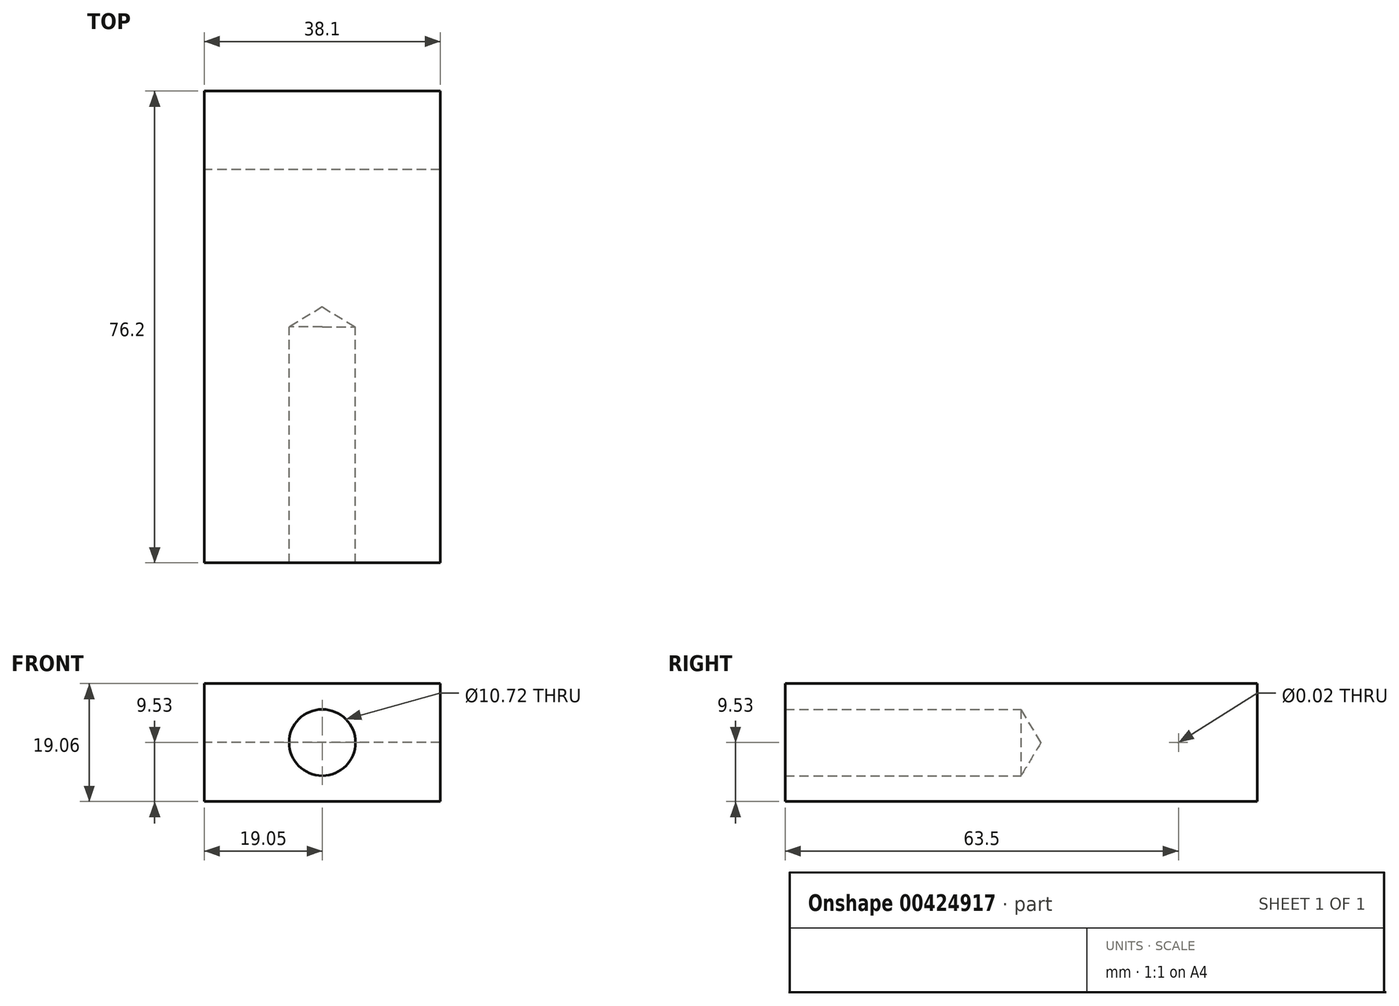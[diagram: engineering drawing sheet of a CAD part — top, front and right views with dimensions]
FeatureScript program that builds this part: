
annotation { "Feature Type Name" : "Feature", "Feature Type Description" : "" }
export const myFeature = defineFeature(function(context is Context, id is Id, definition is map)
    precondition{}
    {
        {
            var Q0;
            Q0=qCreatedBy(makeId("Front.planeOp"),FACE);
            var sketch = newSketch(context, id + "F0", { "sketchPlane" : qUnion([Q0])});
            skLineSegment(sketch, "E0.bottom", {"start": v(19.05, -9.52) * mm, "end": v(-19.05, -9.53) * mm});
            skLineSegment(sketch, "E0.top", {"start": v(19.05, 9.53) * mm, "end": v(-19.05, 9.53) * mm});
            skLineSegment(sketch, "E0.left", {"start": v(19.05, -9.52) * mm, "end": v(19.05, 9.53) * mm});
            skLineSegment(sketch, "E0.right", {"start": v(-19.05, -9.53) * mm, "end": v(-19.05, 9.53) * mm});
            skPoint(sketch, "E0.middle", {"position": v(0, 0) * mm});
            skSolve(sketch);
        }
        {
            var Q0;
            Q0=makeQuery(id+"F0.imprint","IMPRINT",FACE,{"disambiguationData":[TD([[makeQuery(id+"F0.imprint","IMPRINT",EDGE,{"derivedFrom":sQuery(id+"F0.wireOp",EDGE,"E0.bottom")}),-1.0]])]});
            extrude(context, id + "F1", {"entities" : qUnion([Q0]), "depth" : 76.2 * mm, "symmetric" : true});
        }
        {
            var Q0;
            Q0=makeQuery(id+"F1.opExtrude","SWEPT_FACE",FACE,{"disambiguationData":[OSD([sQuery(id+"F0.wireOp",EDGE,"E0.left")])]});
            var sketch = newSketch(context, id + "F2", { "sketchPlane" : qUnion([Q0])});
            skPoint(sketch, "E1", {"position": v(25.4, 0) * mm});
            skSolve(sketch);
        }
        {
            var Q0;
            Q0=makeQuery(id+"F1.opExtrude","CAP_FACE",FACE,{"disambiguationData":[OSD([sQuery(id+"F0.wireOp",EDGE,"E0.bottom"),sQuery(id+"F0.wireOp",EDGE,"E0.top"),sQuery(id+"F0.wireOp",EDGE,"E0.left"),sQuery(id+"F0.wireOp",EDGE,"E0.right")])],"isStart":false});
            var sketch = newSketch(context, id + "F3", { "sketchPlane" : qUnion([Q0])});
            skPoint(sketch, "E2", {"position": v(0, 0) * mm});
            skSolve(sketch);
        }
        {
            var Q0;
            Q0=sQuery(id+"F3.wireOp",VERTEX,"E2");
            var Q1;
            Q1=makeQuery(id+"F1.opExtrude","SWEPT_BODY",BODY,{"disambiguationData":[OSD([sQuery(id+"F0.wireOp",EDGE,"E0.bottom"),sQuery(id+"F0.wireOp",EDGE,"E0.top"),sQuery(id+"F0.wireOp",EDGE,"E0.left"),sQuery(id+"F0.wireOp",EDGE,"E0.right")])]});
            hole(context, id + "F4", {"style" : HoleStyle.SIMPLE, "endStyle" : HoleEndStyle.BLIND, "standardTappedOrClearance" : lookupTablePath({ "standard" : "ANSI", "engagement" : "75%", "pitch" : "13 tpi", "size" : "1/2", "type" : "Tapped" }), "standardBlindInLast" : lookupTablePath({ "standard" : "ANSI", "engagement" : "75%", "pitch" : "13 tpi", "size" : "1/2", "type" : "Tapped" }), "holeDiameter" : 10.72 * mm, "showTappedDepth" : true, "holeDepth" : 38.1 * mm, "isTappedThrough" : true, "tappedDepth" : 32.24 * mm, "tapClearance" : 3, "locations" : qUnion([Q0]), "scope" : qUnion([Q1]), "majorDiameter" : 12.7 * mm, "startStyle" : HoleStartStyle.SKETCH});
        }
        {
            var Q0;
            Q0=sQuery(id+"F2.wireOp",VERTEX,"E1");
            var Q1;
            Q1=makeQuery(id+"F1.opExtrude","SWEPT_BODY",BODY,{"disambiguationData":[OSD([sQuery(id+"F0.wireOp",EDGE,"E0.bottom"),sQuery(id+"F0.wireOp",EDGE,"E0.top"),sQuery(id+"F0.wireOp",EDGE,"E0.left"),sQuery(id+"F0.wireOp",EDGE,"E0.right")])]});
            hole(context, id + "F5", {"style" : HoleStyle.SIMPLE, "endStyle" : HoleEndStyle.THROUGH, "standardTappedOrClearance" : lookupTablePath({ "standard" : "ANSI", "size" : "1/2 (0.5)", "type" : "Drilled" }), "standardBlindInLast" : lookupTablePath({ "standard" : "ANSI", "size" : "1/2", "type" : "Drilled" }), "holeDiameter" : 1 / 50.8 * mm, "isTappedThrough" : true, "tappedDepth" : 32.24 * mm, "tapClearance" : 3, "locations" : qUnion([Q0]), "scope" : qUnion([Q1]), "startStyle" : HoleStartStyle.SKETCH});
        }
    });
